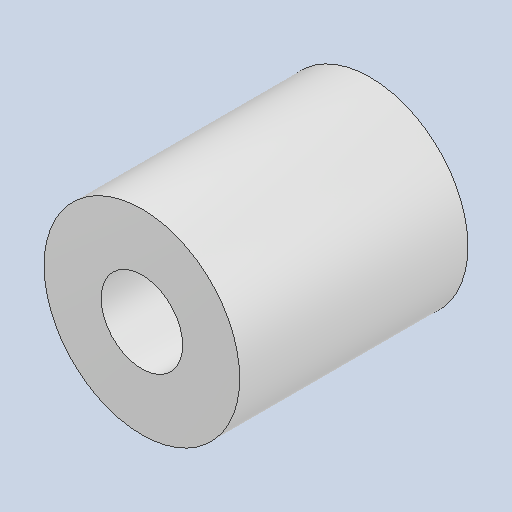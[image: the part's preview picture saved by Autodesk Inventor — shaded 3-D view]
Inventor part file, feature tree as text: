
AUTODESK INVENTOR PART (.ipt)
format: ipt  version: 2023 (Build 270158000, 158)  size: 207,872 bytes
history: native  units: mm
features: extrude x1, sketch x1
ambient origin geometry x8: Origin, YZ Plane, XZ Plane, XY Plane, X Axis, Y Axis, Z Axis, Center Point
bodies: Solid1 (feature_tree)
feature tree (2):
  extrude  "Extrusion1"  Depth=7.0mm
  sketch  "Sketch1"  dims[d0=2.5mm d1=6.0mm d2=7.0mm d3=0.0mm]
